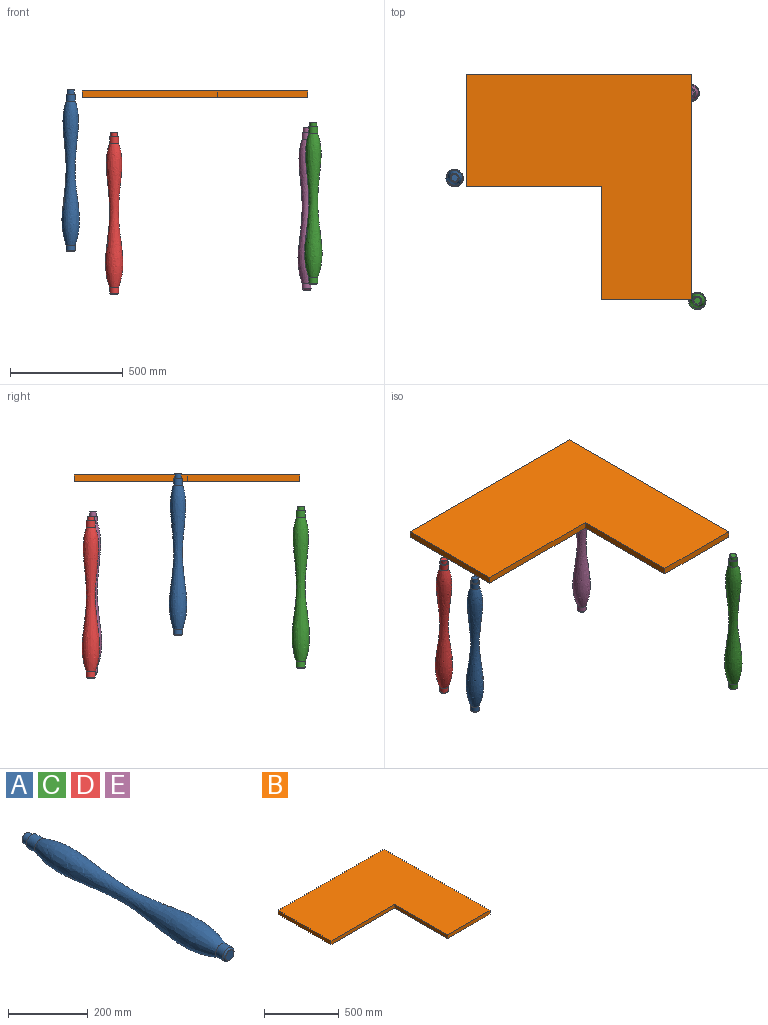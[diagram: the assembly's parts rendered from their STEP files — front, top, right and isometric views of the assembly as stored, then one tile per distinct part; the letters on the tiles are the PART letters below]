
ASSEMBLY  parts=5 mates=1
PART A: 8 faces, bbox 77.8x720x77.8 mm
  f0: plane 40x40mm, normal (0,1,0), area 549.8mm2, adj f1,f6
  f1: cylinder r=20mm len=40mm, axis (0,1,0), area 3769.9mm2, adj f0,f2
  f2: revolved ~640x77.81mm, area 117329.2mm2, adj f1,f3
  f3: cylinder r=20mm len=40mm, axis (0,1,0), area 3141.6mm2, adj f2,f4
  f4: cone r=20mm half-angle=45deg, axis (0,1,0), area 777.5mm2, adj f3,f5
  f5: plane 30x30mm, normal (0,-1,0), area 706.9mm2, adj f4
  f6: cylinder r=15mm len=30mm, axis (0,-1,0), area 1885mm2, adj f0,f7
  f7: plane 30x30mm, normal (0,1,0), area 706.9mm2, adj f6
PART B: 16 faces, bbox 1000x1000x30 mm
  f0: plane 1000x30mm, normal (0,1,0), area 30000mm2, adj f1,f5,f6,f7
  f1: plane 500x30mm, normal (-1,0,0), area 15000mm2, adj f0,f2,f6,f7
  f2: plane 600x30mm, normal (0,-1,0), area 18000mm2, adj f1,f3,f6,f7
  f3: plane 500x30mm, normal (-1,0,0), area 15000mm2, adj f2,f4,f6,f7
  f4: plane 400x30mm, normal (0,-1,0), area 12000mm2, adj f3,f5,f6,f7
  f5: plane 1000x30mm, normal (1,0,0), area 30000mm2, adj f0,f4,f6,f7
  f6: plane 1000x1000mm, normal (0,0,1), area 700000mm2, adj f0,f1,f2,f3,f4,f5
  f7: plane 1000x1000mm, normal (0,0,-1), area 697172.6mm2, adj f0,f1,f2,f3,f4,f5,f8,f10
  f8: cylinder r=15mm len=30mm, axis (0,0,-1), area 1885mm2, adj f7,f9
  f9: plane 30x30mm, normal (0,0,-1), area 706.9mm2, adj f8
  f10: cylinder r=15mm len=30mm, axis (0,0,-1), area 1885mm2, adj f7,f11
  f11: plane 30x30mm, normal (0,0,-1), area 706.9mm2, adj f10
  f12: cylinder r=15mm len=30mm, axis (0,0,-1), area 1885mm2, adj f7,f13
  f13: plane 30x30mm, normal (0,0,-1), area 706.9mm2, adj f12
  f14: cylinder r=15mm len=30mm, axis (0,0,-1), area 1885mm2, adj f7,f15
  f15: plane 30x30mm, normal (0,0,-1), area 706.9mm2, adj f14
PART C: same geometry as A
PART D: same geometry as A
PART E: same geometry as A
PLACE A rot(axis=(1,0,0),90deg) t=(-380.24,70.76,-425.87)mm
PLACE B t=(-75.83,-123.66,-88.86)mm
PLACE C rot(axis=(1,0,0),90deg) t=(696.98,-474.24,-569.53)mm
PLACE D rot(axis=(1,0,0),90deg) t=(-187.32,457.84,-613.55)mm
PLACE E rot(axis=(1,0,0),90deg) t=(667.76,448.89,-595.14)mm
MATE pin_slot A.f4 <-> B.f10  axis (0,0,1) through (-525.06,70.76,-88.86)mm
